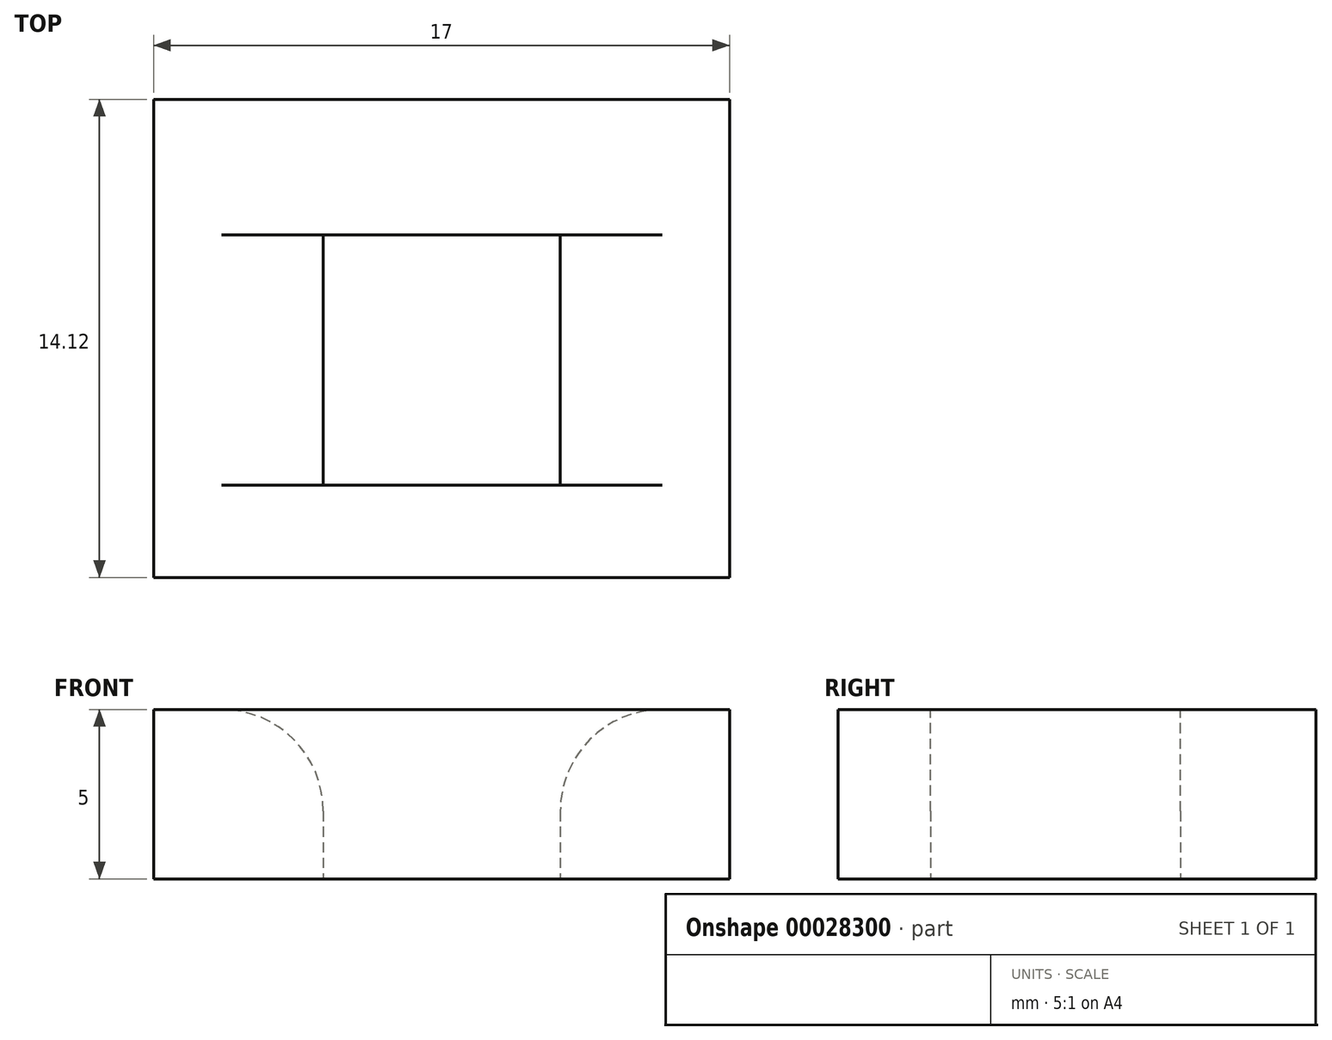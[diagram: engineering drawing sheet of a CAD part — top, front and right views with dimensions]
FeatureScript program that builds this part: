
annotation { "Feature Type Name" : "Feature", "Feature Type Description" : "" }
export const myFeature = defineFeature(function(context is Context, id is Id, definition is map)
    precondition{}
    {
        {
            var Q0;
            Q0=qCreatedBy(makeId("Top.planeOp"),FACE);
            var sketch = newSketch(context, id + "F0", { "sketchPlane" : qUnion([Q0])});
            skLineSegment(sketch, "E0", {"start": v(-8.68, -1.22) * mm, "end": v(-8.68, -12.6) * mm});
            skLineSegment(sketch, "E1", {"start": v(-3.68, -12.6) * mm, "end": v(-3.68, -5.22) * mm});
            skLineSegment(sketch, "E2", {"start": v(-3.68, -5.22) * mm, "end": v(3.32, -5.22) * mm});
            skLineSegment(sketch, "E3", {"start": v(3.32, -5.22) * mm, "end": v(3.32, -12.6) * mm});
            skLineSegment(sketch, "E4", {"start": v(8.32, -12.6) * mm, "end": v(8.32, -1.22) * mm});
            skLineSegment(sketch, "E5", {"start": v(8.32, -1.22) * mm, "end": v(-8.68, -1.22) * mm});
            skLineSegment(sketch, "E6", {"start": v(-8.68, -12.6) * mm, "end": v(-8.68, -15.34) * mm});
            skLineSegment(sketch, "E7", {"start": v(-8.68, -15.34) * mm, "end": v(8.32, -15.34) * mm});
            skLineSegment(sketch, "E8", {"start": v(8.32, -15.34) * mm, "end": v(8.32, -12.6) * mm});
            skLineSegment(sketch, "E9", {"start": v(3.32, -12.6) * mm, "end": v(-3.68, -12.6) * mm});
            skSolve(sketch);
        }
        {
            var Q0;
            Q0=makeQuery(id+"F0.imprint","IMPRINT",FACE,{"disambiguationData":[TD([[makeQuery(id+"F0.imprint","IMPRINT",EDGE,{"derivedFrom":sQuery(id+"F0.wireOp",EDGE,"E0")}),1.0]])]});
            extrude(context, id + "F1", {"entities" : qUnion([Q0]), "depth" : 5 * mm});
        }
        {
            var Q0;
            Q0=makeQuery(id+"F1.opExtrude","CAP_EDGE",EDGE,{"disambiguationData":[OSD([sQuery(id+"F0.wireOp",EDGE,"E1")])],"isStart":false});
            var Q1;
            Q1=makeQuery(id+"F1.opExtrude","CAP_EDGE",EDGE,{"disambiguationData":[OSD([sQuery(id+"F0.wireOp",EDGE,"E3")])],"isStart":false});
            fillet(context, id + "F2", {"entities" : qUnion([Q0, Q1]), "radius" : 3 * mm, "tangentPropagation" : true, "allowEdgeOverflow" : false});
        }
    });
